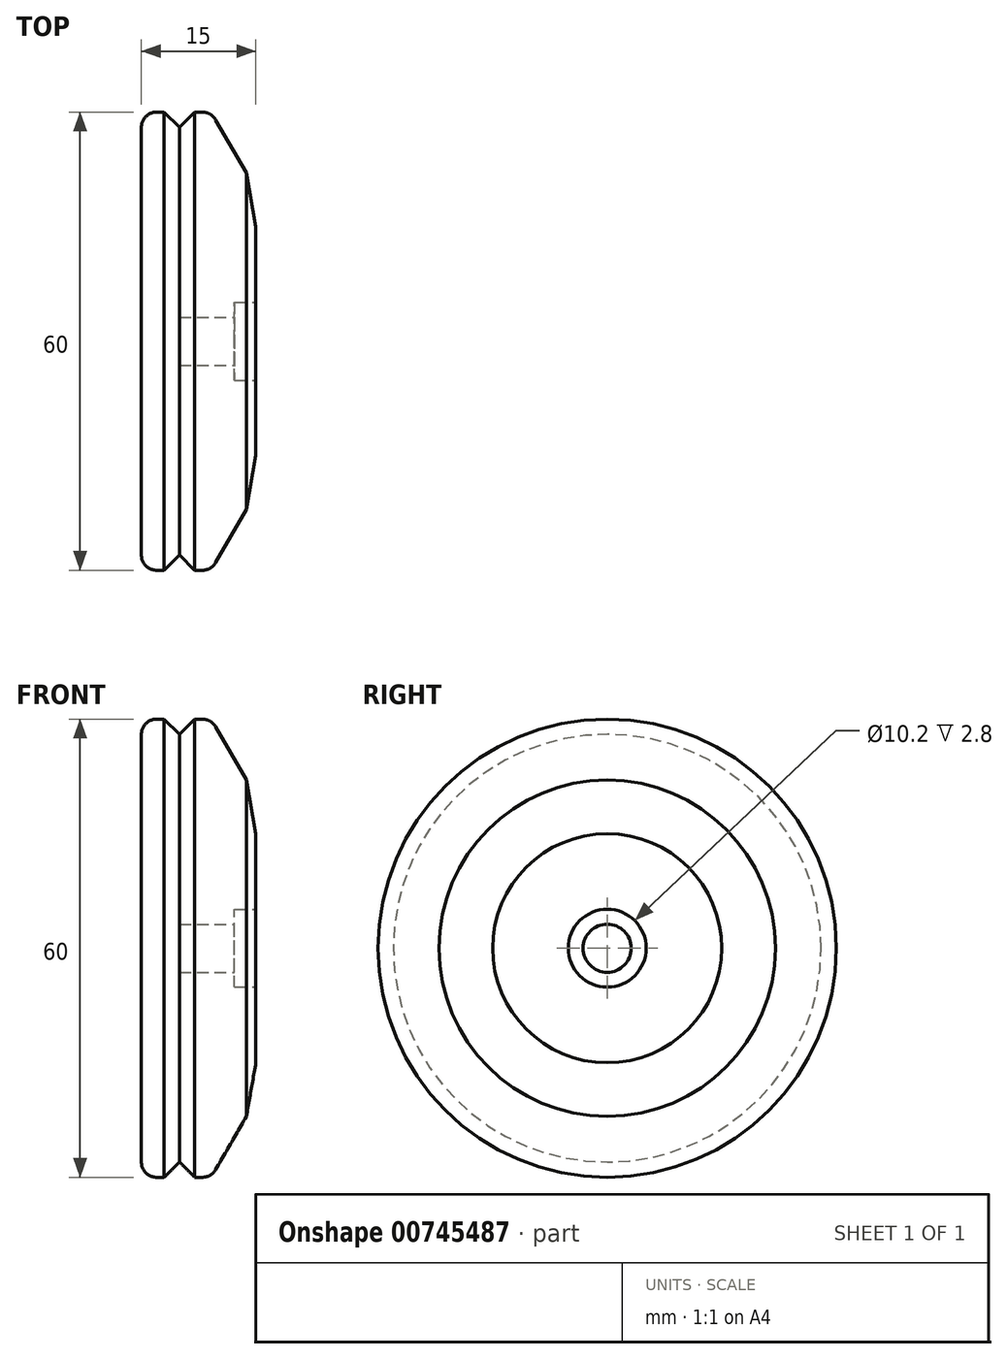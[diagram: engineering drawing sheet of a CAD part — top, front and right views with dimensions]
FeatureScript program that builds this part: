
annotation { "Feature Type Name" : "Feature", "Feature Type Description" : "" }
export const myFeature = defineFeature(function(context is Context, id is Id, definition is map)
    precondition{}
    {
        {
            var Q0;
            Q0=qCreatedBy(makeId("Front.planeOp"),FACE);
            var sketch = newSketch(context, id + "F0", { "sketchPlane" : qUnion([Q0])});
            skLineSegment(sketch, "E0", {"start": v(0, 0) * mm, "end": v(0, 28) * mm});
            skLineSegment(sketch, "E1", {"start": v(2, 30) * mm, "end": v(3, 30) * mm});
            skLineSegment(sketch, "E2", {"start": v(3, 30) * mm, "end": v(5, 28) * mm});
            skLineSegment(sketch, "E3", {"start": v(5, 28) * mm, "end": v(7, 30) * mm});
            skLineSegment(sketch, "E4", {"start": v(7, 30) * mm, "end": v(8, 30) * mm});
            skLineSegment(sketch, "E5", {"start": v(9.73, 29) * mm, "end": v(13.76, 22.02) * mm});
            skLineSegment(sketch, "E6", {"start": v(13.76, 22.02) * mm, "end": v(15, 15) * mm});
            skLineSegment(sketch, "E7", {"start": v(15, 15) * mm, "end": v(15, 5.1) * mm});
            skLineSegment(sketch, "E8", {"start": v(15, 5.1) * mm, "end": v(12.2, 5.1) * mm});
            skLineSegment(sketch, "E9", {"start": v(12.2, 5.1) * mm, "end": v(12.2, 3.15) * mm});
            skLineSegment(sketch, "E10", {"start": v(12.2, 3.15) * mm, "end": v(5, 3.15) * mm});
            skLineSegment(sketch, "E11", {"start": v(5, 3.15) * mm, "end": v(5, 0) * mm});
            skLineSegment(sketch, "E12", {"start": v(5, 0) * mm, "end": v(0, 0) * mm});
            skPoint(sketch, "E13.visualSharp", {"position": v(0, 30) * mm});
            skArc(sketch, "E13.filletArc", {"start": v(2, 30) * mm, "mid": v(0.59, 29.41) * mm, "end": v(0, 28) * mm});
            skPoint(sketch, "E14.visualSharp", {"position": v(9.15, 30) * mm});
            skArc(sketch, "E14.filletArc", {"start": v(9.73, 29) * mm, "mid": v(9, 29.73) * mm, "end": v(8, 30) * mm});
            skSolve(sketch);
        }
        {
            var Q0;
            Q0=makeQuery(id+"F0.imprint","IMPRINT",FACE,{"disambiguationData":[TD([[makeQuery(id+"F0.imprint","IMPRINT",EDGE,{"derivedFrom":sQuery(id+"F0.wireOp",EDGE,"E0")}),-1.0]])]});
            var Q1;
            Q1=sQuery(id+"F0.wireOp",EDGE,"E12");
            revolve(context, id + "F1", {"surfaceOperationType" : NewSurfaceOperationType.NEW, "entities" : qUnion([Q0]), "axis" : qUnion([Q1]), "revolveType" : RevolveType.FULL});
        }
    });
